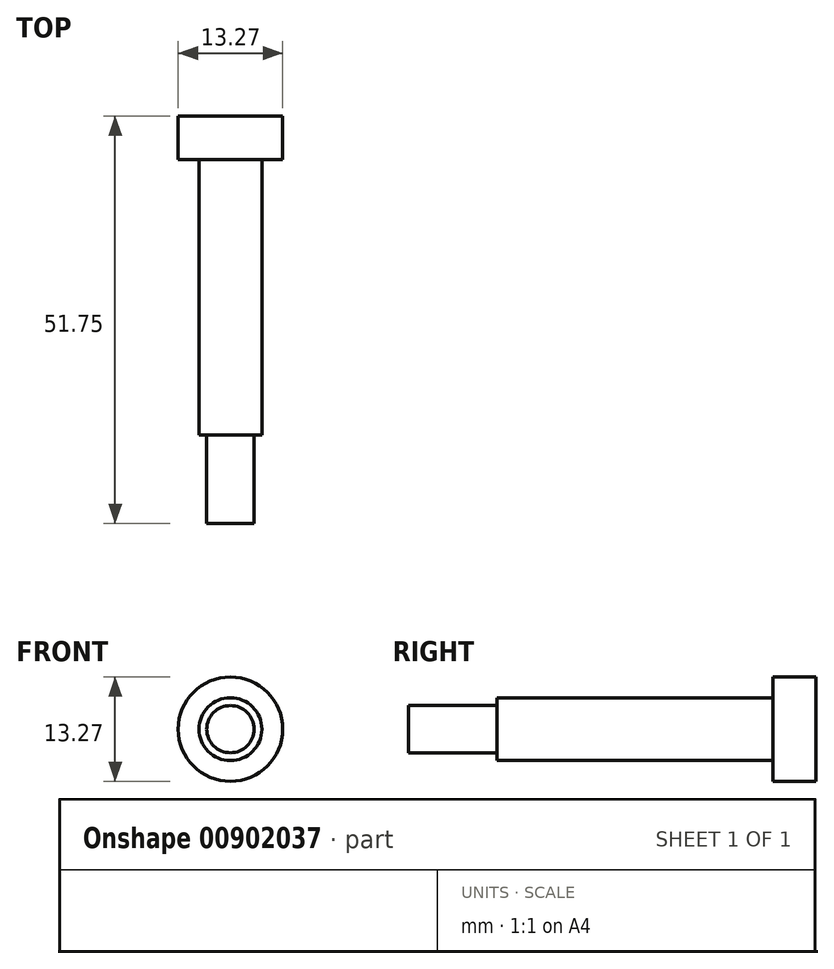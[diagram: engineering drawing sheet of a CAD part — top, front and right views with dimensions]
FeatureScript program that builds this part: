
annotation { "Feature Type Name" : "Feature", "Feature Type Description" : "" }
export const myFeature = defineFeature(function(context is Context, id is Id, definition is map)
    precondition{}
    {
        {
            var Q0;
            Q0=qCreatedBy(makeId("Front.planeOp"),FACE);
            var sketch = newSketch(context, id + "F0", { "sketchPlane" : qUnion([Q0])});
            skCircle(sketch, "E0", {"center": v(-35.83, 14.8) * mm, "radius": 6.64 * mm});
            skSolve(sketch);
        }
        {
            var Q0;
            Q0=makeQuery(id+"F0.imprint","IMPRINT",FACE,{"disambiguationData":[TD([[makeQuery(id+"F0.imprint","IMPRINT",EDGE,{"derivedFrom":sQuery(id+"F0.wireOp",EDGE,"E0")}),1.0]])]});
            extrude(context, id + "F1", {"entities" : qUnion([Q0]), "depth" : 5.5 * mm, "offsetDistance" : 25 * mm});
        }
        {
            var Q0;
            Q0=makeQuery(id+"F1.opExtrude","CAP_FACE",FACE,{"disambiguationData":[OSD([sQuery(id+"F0.wireOp",EDGE,"E0")])],"isStart":false});
            var sketch = newSketch(context, id + "F2", { "sketchPlane" : qUnion([Q0])});
            skCircle(sketch, "E1", {"center": v(-35.83, 14.8) * mm, "radius": 4 * mm});
            skSolve(sketch);
        }
        {
            var Q0;
            Q0=makeQuery(id+"F2.imprint","IMPRINT",FACE,{"disambiguationData":[TD([[makeQuery(id+"F2.imprint","IMPRINT",EDGE,{"derivedFrom":sQuery(id+"F2.wireOp",EDGE,"E1")}),1.0]])]});
            var Q1;
            Q1=sQuery(id+"F2.wireOp",EDGE,"E1");
            extrude(context, id + "F3", {"entities" : qUnion([Q0]), "operationType" : NewBodyOperationType.ADD, "surfaceOperationType" : NewSurfaceOperationType.ADD, "surfaceEntities" : qUnion([Q1]), "depth" : 35 * mm, "offsetDistance" : 25 * mm});
        }
        {
            var Q0;
            Q0=makeQuery(id+"F3.opExtrude","CAP_FACE",FACE,{"disambiguationData":[OSD([sQuery(id+"F2.wireOp",EDGE,"E1")])],"isStart":false});
            var sketch = newSketch(context, id + "F4", { "sketchPlane" : qUnion([Q0])});
            skCircle(sketch, "E2", {"center": v(-35.83, 14.8) * mm, "radius": 3 * mm});
            skSolve(sketch);
        }
        {
            var Q0;
            Q0=makeQuery(id+"F4.imprint","IMPRINT",FACE,{"disambiguationData":[TD([[makeQuery(id+"F4.imprint","IMPRINT",EDGE,{"derivedFrom":sQuery(id+"F4.wireOp",EDGE,"E2")}),1.0]])]});
            extrude(context, id + "F5", {"entities" : qUnion([Q0]), "operationType" : NewBodyOperationType.ADD, "depth" : 11.25 * mm, "offsetDistance" : 25 * mm});
        }
    });
